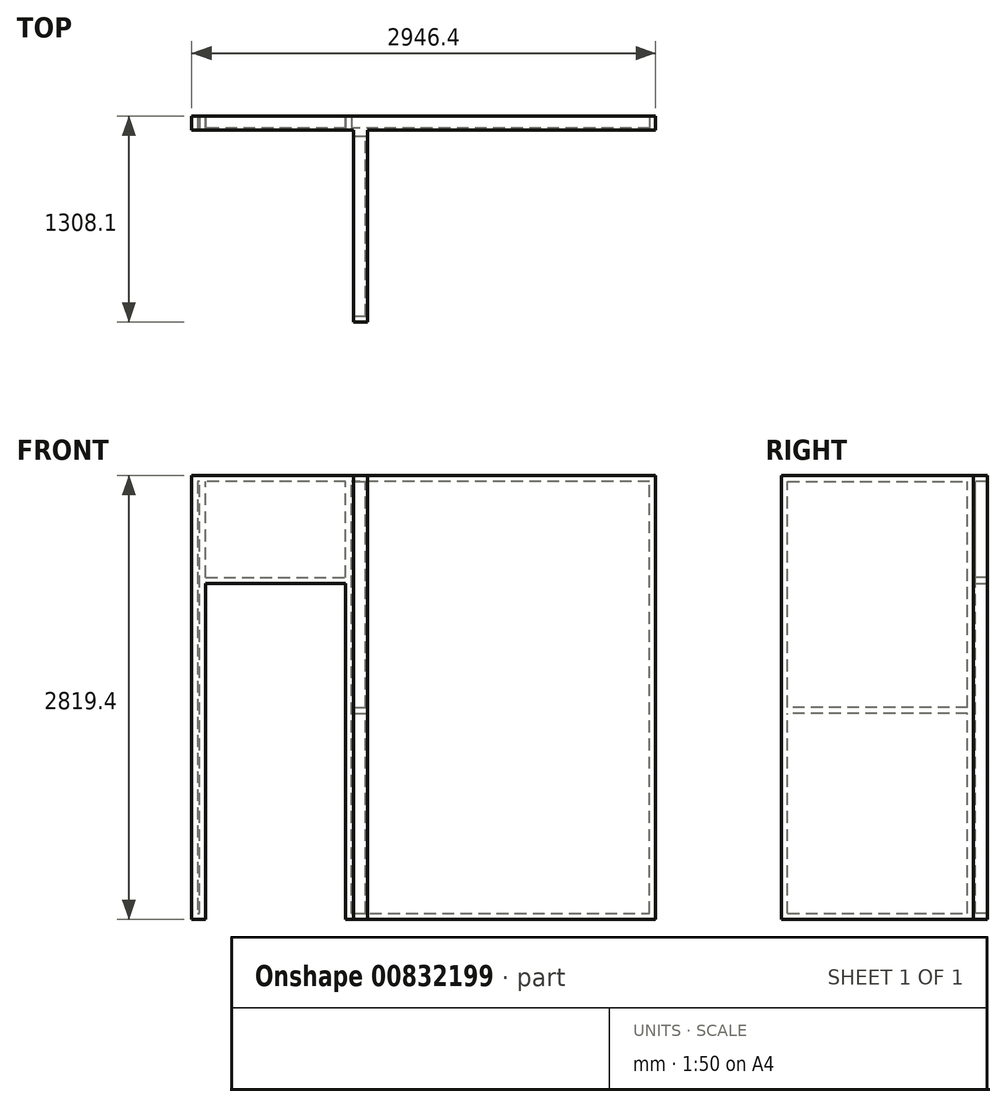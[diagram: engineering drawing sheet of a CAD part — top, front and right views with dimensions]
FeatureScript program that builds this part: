
annotation { "Feature Type Name" : "Feature", "Feature Type Description" : "" }
export const myFeature = defineFeature(function(context is Context, id is Id, definition is map)
    precondition{}
    {
        {
            var Q0;
            Q0=qCreatedBy(makeId("Front.planeOp"),FACE);
            var sketch = newSketch(context, id + "F0", { "sketchPlane" : qUnion([Q0])});
            skLineSegment(sketch, "E0.bottom", {"start": v(1473.2, 1409.7) * mm, "end": v(-1473.2, 1409.7) * mm});
            skLineSegment(sketch, "E0.top", {"start": v(1473.2, -1409.7) * mm, "end": v(-495.3, -1409.7) * mm});
            skLineSegment(sketch, "E0.left", {"start": v(1473.2, 1409.7) * mm, "end": v(1473.2, -1409.7) * mm});
            skLineSegment(sketch, "E0.right", {"start": v(-1473.2, 1409.7) * mm, "end": v(-1473.2, -1409.7) * mm});
            skPoint(sketch, "E0.middle", {"position": v(0, 0) * mm});
            skLineSegment(sketch, "E1.top", {"start": v(-1384.3, 723.9) * mm, "end": v(-495.3, 723.9) * mm});
            skLineSegment(sketch, "E1.left", {"start": v(-1384.3, -1409.7) * mm, "end": v(-1384.3, 723.9) * mm});
            skLineSegment(sketch, "E1.right", {"start": v(-495.3, -1409.7) * mm, "end": v(-495.3, 723.9) * mm});
            skLineSegment(sketch, "E2.trimOffspring", {"start": v(-1384.3, -1409.7) * mm, "end": v(-1473.2, -1409.7) * mm});
            skSolve(sketch);
        }
        {
            var Q0;
            Q0=qSketchRegion(id+"F0",true);
            extrude(context, id + "F1", {"entities" : qUnion([Q0]), "depth" : 12.7 * mm, "offsetDistance" : 25.4 * mm});
        }
        {
            var Q0;
            Q0=makeQuery(id+"F1.opExtrude","CAP_FACE",FACE,{"disambiguationData":[OSD([sQuery(id+"F0.wireOp",EDGE,"E0.bottom"),sQuery(id+"F0.wireOp",EDGE,"E0.top"),sQuery(id+"F0.wireOp",EDGE,"E0.left"),sQuery(id+"F0.wireOp",EDGE,"E0.right"),sQuery(id+"F0.wireOp",EDGE,"E1.top"),sQuery(id+"F0.wireOp",EDGE,"E1.left"),sQuery(id+"F0.wireOp",EDGE,"E1.right"),sQuery(id+"F0.wireOp",EDGE,"E2.trimOffspring")])],"isStart":true});
            var sketch = newSketch(context, id + "F2", { "sketchPlane" : qUnion([Q0])});
            skLineSegment(sketch, "E3.bottom", {"start": v(-1473.2, 1409.7) * mm, "end": v(1473.2, 1409.7) * mm});
            skLineSegment(sketch, "E3.top", {"start": v(-1473.2, 1371.6) * mm, "end": v(1473.2, 1371.6) * mm});
            skLineSegment(sketch, "E3.left", {"start": v(-1473.2, 1409.7) * mm, "end": v(-1473.2, 1371.6) * mm});
            skLineSegment(sketch, "E3.right", {"start": v(1473.2, 1409.7) * mm, "end": v(1473.2, 1371.6) * mm});
            skLineSegment(sketch, "E4.bottom", {"start": v(1473.2, 1371.6) * mm, "end": v(1435.1, 1371.6) * mm});
            skLineSegment(sketch, "E4.top", {"start": v(1473.2, -1371.6) * mm, "end": v(1435.1, -1371.6) * mm});
            skLineSegment(sketch, "E4.left", {"start": v(1473.2, 1371.6) * mm, "end": v(1473.2, -1371.6) * mm});
            skLineSegment(sketch, "E4.right", {"start": v(1435.1, 1371.6) * mm, "end": v(1435.1, -1371.6) * mm});
            skLineSegment(sketch, "E5.bottom", {"start": v(1473.2, -1371.6) * mm, "end": v(1384.3, -1371.6) * mm});
            skLineSegment(sketch, "E5.top", {"start": v(1473.2, -1409.7) * mm, "end": v(1384.3, -1409.7) * mm});
            skLineSegment(sketch, "E5.left", {"start": v(1473.2, -1371.6) * mm, "end": v(1473.2, -1409.7) * mm});
            skLineSegment(sketch, "E5.right", {"start": v(1384.3, -1371.6) * mm, "end": v(1384.3, -1409.7) * mm});
            skLineSegment(sketch, "E6.bottom", {"start": v(1384.3, -1371.6) * mm, "end": v(1422.4, -1371.6) * mm});
            skLineSegment(sketch, "E6.top", {"start": v(1384.3, 1371.6) * mm, "end": v(1422.4, 1371.6) * mm});
            skLineSegment(sketch, "E6.left", {"start": v(1384.3, -1371.6) * mm, "end": v(1384.3, 1371.6) * mm});
            skLineSegment(sketch, "E6.right", {"start": v(1422.4, -1371.6) * mm, "end": v(1422.4, 1371.6) * mm});
            skLineSegment(sketch, "E7.bottom", {"start": v(1384.3, 762) * mm, "end": v(495.3, 762) * mm});
            skLineSegment(sketch, "E7.top", {"start": v(1384.3, 723.9) * mm, "end": v(495.3, 723.9) * mm});
            skLineSegment(sketch, "E7.left", {"start": v(1384.3, 762) * mm, "end": v(1384.3, 723.9) * mm});
            skLineSegment(sketch, "E7.right", {"start": v(495.3, 762) * mm, "end": v(495.3, 723.9) * mm});
            skLineSegment(sketch, "E8.bottom", {"start": v(495.3, -1409.7) * mm, "end": v(-1473.2, -1409.7) * mm});
            skLineSegment(sketch, "E8.top", {"start": v(495.3, -1371.6) * mm, "end": v(-1473.2, -1371.6) * mm});
            skLineSegment(sketch, "E8.left", {"start": v(495.3, -1409.7) * mm, "end": v(495.3, -1371.6) * mm});
            skLineSegment(sketch, "E8.right", {"start": v(-1473.2, -1409.7) * mm, "end": v(-1473.2, -1371.6) * mm});
            skLineSegment(sketch, "E9.bottom", {"start": v(-1473.2, -1371.6) * mm, "end": v(-1435.1, -1371.6) * mm});
            skLineSegment(sketch, "E9.top", {"start": v(-1473.2, 1371.6) * mm, "end": v(-1435.1, 1371.6) * mm});
            skLineSegment(sketch, "E9.left", {"start": v(-1473.2, -1371.6) * mm, "end": v(-1473.2, 1371.6) * mm});
            skLineSegment(sketch, "E9.right", {"start": v(-1435.1, -1371.6) * mm, "end": v(-1435.1, 1371.6) * mm});
            skLineSegment(sketch, "E10.bottom", {"start": v(-1079.5, 1371.6) * mm, "end": v(-1041.4, 1371.6) * mm});
            skLineSegment(sketch, "E10.top", {"start": v(-1079.5, -1371.6) * mm, "end": v(-1041.4, -1371.6) * mm});
            skLineSegment(sketch, "E10.left", {"start": v(-1079.5, 1371.6) * mm, "end": v(-1079.5, -1371.6) * mm});
            skLineSegment(sketch, "E10.right", {"start": v(-1041.4, 1371.6) * mm, "end": v(-1041.4, -1371.6) * mm});
            skLineSegment(sketch, "E11.bottom", {"start": v(495.3, -1371.6) * mm, "end": v(457.2, -1371.6) * mm});
            skLineSegment(sketch, "E11.top", {"start": v(495.3, 1371.6) * mm, "end": v(457.2, 1371.6) * mm});
            skLineSegment(sketch, "E11.left", {"start": v(495.3, -1371.6) * mm, "end": v(495.3, 1371.6) * mm});
            skLineSegment(sketch, "E11.right", {"start": v(457.2, -1371.6) * mm, "end": v(457.2, 1371.6) * mm});
            skLineSegment(sketch, "E12.bottom", {"start": v(1041.4, 1371.6) * mm, "end": v(1079.5, 1371.6) * mm});
            skLineSegment(sketch, "E12.top", {"start": v(1041.4, -1371.6) * mm, "end": v(1079.5, -1371.6) * mm});
            skLineSegment(sketch, "E13.bottom", {"start": v(901.7, 1371.6) * mm, "end": v(939.8, 1371.6) * mm});
            skLineSegment(sketch, "E13.top", {"start": v(901.7, 762) * mm, "end": v(939.8, 762) * mm});
            skLineSegment(sketch, "E13.left", {"start": v(901.7, 1371.6) * mm, "end": v(901.7, 762) * mm});
            skLineSegment(sketch, "E13.right", {"start": v(939.8, 1371.6) * mm, "end": v(939.8, 762) * mm});
            skLineSegment(sketch, "E14.bottom", {"start": v(-279.4, 1371.6) * mm, "end": v(-317.5, 1371.6) * mm});
            skLineSegment(sketch, "E14.top", {"start": v(-279.4, -1371.6) * mm, "end": v(-317.5, -1371.6) * mm});
            skLineSegment(sketch, "E14.left", {"start": v(-279.4, 1371.6) * mm, "end": v(-279.4, -1371.6) * mm});
            skLineSegment(sketch, "E14.right", {"start": v(-317.5, 1371.6) * mm, "end": v(-317.5, -1371.6) * mm});
            skSolve(sketch);
        }
        {
            var Q0;
            Q0 = qSketchRegion(id + "F2", true);
            var Q1;
            Q1=makeQuery(id+"F2.imprint","IMPRINT",FACE,{"disambiguationData":[TD([[makeQuery(id+"F2.imprint","IMPRINT",EDGE,{"derivedFrom":sQuery(id+"F2.wireOp",EDGE,"E10.bottom")}),-1.0]])]});
            var Q2;
            Q2=makeQuery(id+"F2.imprint","IMPRINT",FACE,{"disambiguationData":[TD([[makeQuery(id+"F2.imprint","IMPRINT",EDGE,{"derivedFrom":sQuery(id+"F2.wireOp",EDGE,"E14.bottom")}),1.0]])]});
            var Q3;
            Q3=makeQuery(id+"F2.imprint","IMPRINT",FACE,{"disambiguationData":[TD([[makeQuery(id+"F2.imprint","IMPRINT",EDGE,{"derivedFrom":sQuery(id+"F2.wireOp",EDGE,"E13.bottom")}),-1.0]])]});
            extrude(context, id + "F3", {"entities" : qUnion([Q0, Q1, Q2, Q3]), "operationType" : NewBodyOperationType.ADD, "depth" : 76.2 * mm, "offsetDistance" : 25.4 * mm});
        }
        {
            var Q0;
            Q0=makeQuery(id+"F1.opExtrude","CAP_FACE",FACE,{"disambiguationData":[OSD([sQuery(id+"F0.wireOp",EDGE,"E0.bottom"),sQuery(id+"F0.wireOp",EDGE,"E0.top"),sQuery(id+"F0.wireOp",EDGE,"E0.left"),sQuery(id+"F0.wireOp",EDGE,"E0.right"),sQuery(id+"F0.wireOp",EDGE,"E1.top"),sQuery(id+"F0.wireOp",EDGE,"E1.left"),sQuery(id+"F0.wireOp",EDGE,"E1.right"),sQuery(id+"F0.wireOp",EDGE,"E2.trimOffspring")])],"isStart":false});
            var sketch = newSketch(context, id + "F4", { "sketchPlane" : qUnion([Q0])});
            skLineSegment(sketch, "E15.bottom", {"start": v(-368.3, -1409.7) * mm, "end": v(-355.6, -1409.7) * mm});
            skLineSegment(sketch, "E15.top", {"start": v(-368.3, 1409.7) * mm, "end": v(-355.6, 1409.7) * mm});
            skLineSegment(sketch, "E15.left", {"start": v(-368.3, -1409.7) * mm, "end": v(-368.3, 1409.7) * mm});
            skLineSegment(sketch, "E15.right", {"start": v(-355.6, -1409.7) * mm, "end": v(-355.6, 1409.7) * mm});
            skSolve(sketch);
        }
        {
            var Q0;
            Q0=makeQuery(id+"F4.imprint","IMPRINT",FACE,{"disambiguationData":[TD([[makeQuery(id+"F4.imprint","IMPRINT",EDGE,{"derivedFrom":sQuery(id+"F4.wireOp",EDGE,"E15.bottom")}),-1.0]])]});
            extrude(context, id + "F5", {"entities" : qUnion([Q0]), "operationType" : NewBodyOperationType.ADD, "depth" : 1219.2 * mm, "offsetDistance" : 25.4 * mm});
        }
        {
            var Q0;
            Q0=makeQuery(id+"F5.opExtrude","SWEPT_FACE",FACE,{"disambiguationData":[OSD([sQuery(id+"F4.wireOp",EDGE,"E15.left")])]});
            var sketch = newSketch(context, id + "F6", { "sketchPlane" : qUnion([Q0])});
            skLineSegment(sketch, "E16.bottom", {"start": v(1231.9, 1409.7) * mm, "end": v(12.7, 1409.7) * mm});
            skLineSegment(sketch, "E16.top", {"start": v(1231.9, 1371.6) * mm, "end": v(12.7, 1371.6) * mm});
            skLineSegment(sketch, "E16.left", {"start": v(1231.9, 1409.7) * mm, "end": v(1231.9, 1371.6) * mm});
            skLineSegment(sketch, "E16.right", {"start": v(12.7, 1409.7) * mm, "end": v(12.7, 1371.6) * mm});
            skLineSegment(sketch, "E17.bottom", {"start": v(1231.9, -1409.7) * mm, "end": v(1193.8, -1409.7) * mm});
            skLineSegment(sketch, "E17.top", {"start": v(1231.9, 1371.6) * mm, "end": v(1193.8, 1371.6) * mm});
            skLineSegment(sketch, "E17.left", {"start": v(1231.9, -1409.7) * mm, "end": v(1231.9, 1371.6) * mm});
            skLineSegment(sketch, "E17.right", {"start": v(1193.8, -1409.7) * mm, "end": v(1193.8, 1371.6) * mm});
            skLineSegment(sketch, "E18.bottom", {"start": v(1193.8, -1409.7) * mm, "end": v(12.7, -1409.7) * mm});
            skLineSegment(sketch, "E18.top", {"start": v(1193.8, -1371.6) * mm, "end": v(12.7, -1371.6) * mm});
            skLineSegment(sketch, "E18.left", {"start": v(1193.8, -1409.7) * mm, "end": v(1193.8, -1371.6) * mm});
            skLineSegment(sketch, "E18.right", {"start": v(12.7, -1409.7) * mm, "end": v(12.7, -1371.6) * mm});
            skLineSegment(sketch, "E19.bottom", {"start": v(12.7, -1371.6) * mm, "end": v(50.8, -1371.6) * mm});
            skLineSegment(sketch, "E19.top", {"start": v(12.7, 1371.6) * mm, "end": v(50.8, 1371.6) * mm});
            skLineSegment(sketch, "E19.left", {"start": v(12.7, -1371.6) * mm, "end": v(12.7, 1371.6) * mm});
            skLineSegment(sketch, "E19.right", {"start": v(50.8, -1371.6) * mm, "end": v(50.8, 1371.6) * mm});
            skLineSegment(sketch, "E20.bottom", {"start": v(50.8, -63.5) * mm, "end": v(1193.8, -63.5) * mm});
            skLineSegment(sketch, "E20.top", {"start": v(50.8, -101.6) * mm, "end": v(1193.8, -101.6) * mm});
            skLineSegment(sketch, "E20.left", {"start": v(50.8, -63.5) * mm, "end": v(50.8, -101.6) * mm});
            skLineSegment(sketch, "E20.right", {"start": v(1193.8, -63.5) * mm, "end": v(1193.8, -101.6) * mm});
            skSolve(sketch);
        }
        {
            var Q0;
            Q0 = qSketchRegion(id + "F6", true);
            var Q1;
            Q1=makeQuery(id+"F6.imprint","IMPRINT",FACE,{"disambiguationData":[TD([[makeQuery(id+"F6.imprint","IMPRINT",EDGE,{"derivedFrom":sQuery(id+"F6.wireOp",EDGE,"E20.bottom")}),-1.0]])]});
            extrude(context, id + "F7", {"entities" : qUnion([Q0, Q1]), "operationType" : NewBodyOperationType.ADD, "depth" : 76.2 * mm, "offsetDistance" : 25.4 * mm});
        }
    });
